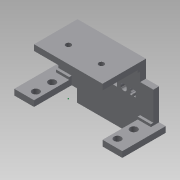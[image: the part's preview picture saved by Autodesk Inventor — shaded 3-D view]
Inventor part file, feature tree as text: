
AUTODESK INVENTOR PART (.ipt)
format: ipt  version: 2015 SP1 (Build 190203100, 203)  size: 549,888 bytes
history: native  units: mm
features: sketch x27, extrude x24, reference x13, projected_geometry x7, mirror x6
ambient origin geometry x8: Origin, YZ Plane, XZ Plane, XY Plane, X Axis, Y Axis, Z Axis, Center Point
bodies: Solid1 (feature_tree)
feature tree (77):
  extrude  "Extrusion1"  Depth=29.21mm
  extrude  "Extrusion2"  Depth=3.5mm
  extrude  "Extrusion3"  Depth=57.15mm TaperAngle=0.0deg
  sketch  "Sketch5"  dims[d8=57.15mm d9=0.0mm d11=25.147mm d12=0.0mm]
  extrude  "Extrusion4"  Depth=25.147mm TaperAngle=0.0deg
  extrude  "Extrusion5"  Depth=21.1822mm
  mirror  "Mirror1"
  extrude  "Extrusion6"  Depth=25.147mm TaperAngle=0.0deg
  extrude  "Extrusion8"  Depth=3.5mm TaperAngle=0.0deg
  extrude  "Extrusion9"  Depth=3.5mm
  extrude  "Extrusion10"  Depth=7.95mm TaperAngle=0.0deg
  sketch  "Sketch16"  dims[d38=7.95mm d39=0.0mm d43=7.95mm d44=0.0mm]
  extrude  "Extrusion11"  Depth=7.95mm TaperAngle=0.0deg
  sketch  "Sketch19"  dims[d47=3.5mm d48=0.0mm d50=2.0mm]
  extrude  "Extrusion12"  Depth=2.0mm
  mirror  "Mirror2"
  extrude  "Extrusion13"  Depth=3.5mm TaperAngle=0.0deg
  extrude  "Extrusion15"  Depth=7.95mm TaperAngle=0.0deg
  sketch  "Sketch24"  dims[d59=3.5mm d60=0.0mm d61=3.5mm d62=0.0mm]
  extrude  "Extrusion17"  Depth=3.5mm TaperAngle=0.0deg
  extrude  "Extrusion18"  Depth=3.5mm TaperAngle=0.0deg
  mirror  "Mirror4"
  extrude  "Extrusion19"  Depth=1.5mm
  extrude  "Extrusion20"  Depth=1.5mm TaperAngle=0.0deg
  sketch  "Sketch29"  dims[d72=1.5mm d73=1.5mm]
  sketch  "Sketch30"  dims[d74=7.95mm d75=0.0mm]
  extrude  "Extrusion21"  Depth=1.5mm
  mirror  "Mirror5"
  extrude  "Extrusion22"  [1 undecoded]
  extrude  "Extrusion23"  [1 undecoded]
  extrude  "Extrusion24"  [1 undecoded]
  mirror  "Mirror6"
  extrude  "Extrusion25"  [1 undecoded]
  sketch  "Sketch35"
  sketch  "Sketch36"
  extrude  "Extrusion26"  [1 undecoded]
  sketch  "Sketch37"
  extrude  "Extrusion27"  [1 undecoded]
  mirror  "Mirror7"
  sketch  "Sketch1"  dims[d0=57.15mm d1=29.21mm]
  sketch  "Sketch2"  dims[d2=3.5mm d3=0.0mm d4=3.5mm]
  sketch  "Sketch4"  dims[d5=3.5mm d6=57.15mm d7=0.0mm]
  sketch  "Sketch9"  dims[d15=25.147mm d16=0.0mm d18=21.1822mm]
  reference  "Reference3"
  reference  "Reference4"
  sketch  "Sketch11"  dims[d19=22.428mm d20=25.147mm d21=0.0mm]
  reference  "Reference7"
  sketch  "Sketch13"  dims[d24=3.5mm d25=0.0mm d26=3.5mm d27=0.0mm]
  sketch  "Sketch14"  dims[d28=3.5mm d29=0.0mm d30=3.5mm]
  sketch  "Sketch15"  dims[d33=22.682mm d34=0.0mm d36=7.95mm d37=0.0mm]
  reference  "Reference24"
  projected_geometry  "Projected Loop1"
  sketch  "Sketch21"  dims[d51=3.5mm d52=0.0mm d53=3.5mm d54=0.0mm]
  projected_geometry  "Projected Loop2"
  sketch  "Sketch23"  dims[d55=3.5mm d56=0.0mm d57=7.95mm d58=0.0mm]
  reference  "Reference26"
  reference  "Reference27"
  reference  "Reference28"
  reference  "Reference29"
  reference  "Reference30"
  sketch  "Sketch26"  dims[d63=3.5mm d64=0.0mm d65=3.5mm d66=0.0mm]
  sketch  "Sketch27"  dims[d67=3.9751mm d68=1.5mm]
  sketch  "Sketch28"  dims[d69=1.5mm d70=41.25mm d71=0.0mm]
  projected_geometry  "Projected Loop3"
  projected_geometry  "Projected Loop4"
  projected_geometry  "Projected Loop5"
  projected_geometry  "Projected Loop6"
  projected_geometry  "Projected Loop7"
  sketch  "Sketch31"
  sketch  "Sketch32"
  reference  "Reference33"
  reference  "Reference34"
  reference  "Reference35"
  reference  "Reference36"
  sketch  "Sketch33"
  sketch  "Sketch34"
  sketch  "Sketch38"
note: 6 required parameter values undecoded (feature->parameter linkage not recoverable at this tier; creation-order binding heuristic only, values carry confidence <= 0.55)
